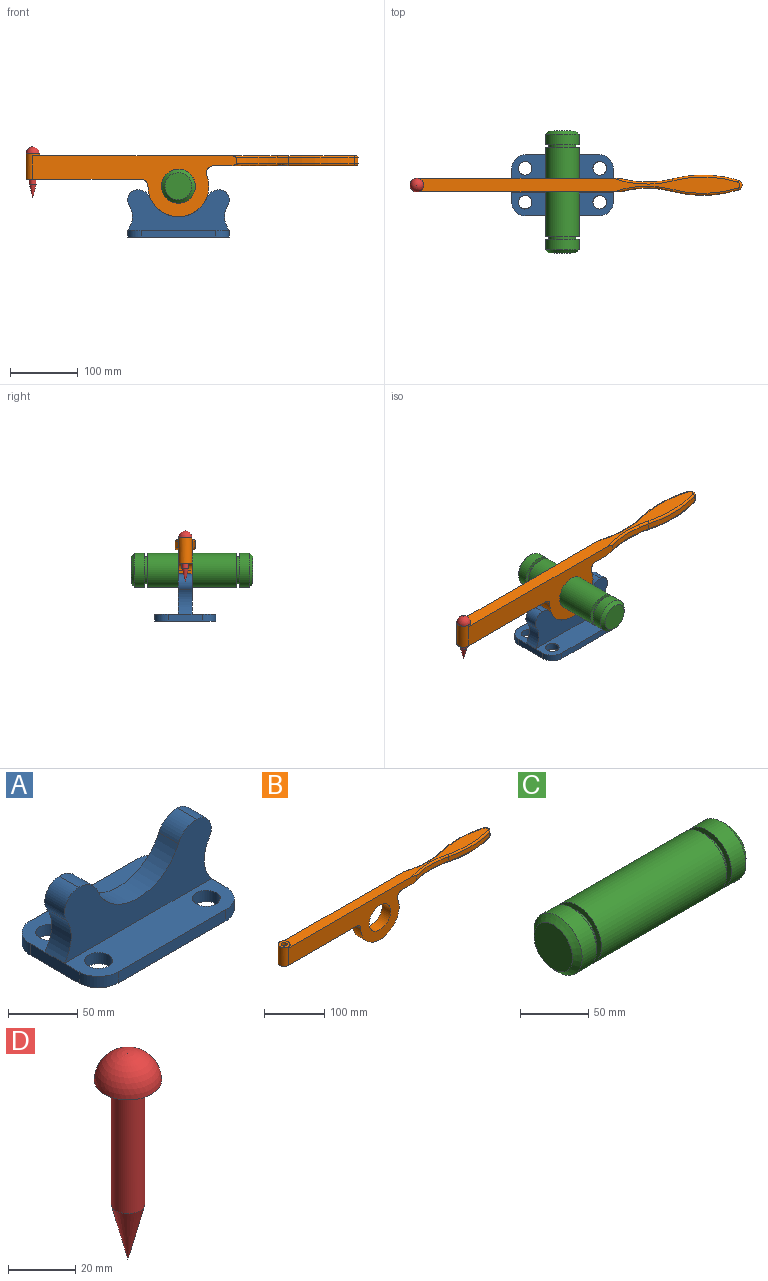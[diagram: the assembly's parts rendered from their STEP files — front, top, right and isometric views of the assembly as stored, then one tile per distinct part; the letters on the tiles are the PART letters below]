
ASSEMBLY  parts=4 mates=4
PART A: 24 faces, bbox 150x90x69.7 mm
  f0: plane 150x35mm, normal (0,0,1), area 4450mm2, adj f1,f2,f3,f4,f5,f8,f9,f23
  f1: plane 50x10mm, normal (1,0,0), area 500mm2, adj f0,f2,f12,f13,f14,f18
  f2: cylinder r=20mm len=20mm, axis (0,0,-1), area 314.2mm2, adj f0,f1,f3,f14
  f3: plane 110x10mm, normal (0,1,0), area 1100mm2, adj f0,f2,f4,f14
  f4: cylinder r=20mm len=20mm, axis (0,0,-1), area 314.2mm2, adj f0,f3,f5,f14
  f5: plane 50x10mm, normal (-1,0,0), area 500mm2, adj f0,f4,f6,f13,f14,f17
  f6: cylinder r=20mm len=20mm, axis (0,0,-1), area 314.2mm2, adj f5,f7,f13,f14
  f7: plane 110x10mm, normal (0,-1,0), area 1100mm2, adj f6,f12,f13,f14
  f8: cylinder r=10mm len=20mm, axis (0,0,-1), area 628.3mm2, adj f0,f14
  f9: cylinder r=10mm len=20mm, axis (0,0,-1), area 628.3mm2, adj f0,f14
  f10: cylinder r=10mm len=20mm, axis (0,0,-1), area 628.3mm2, adj f13,f14
  f11: cylinder r=10mm len=20mm, axis (0,0,-1), area 628.3mm2, adj f13,f14
  f12: cylinder r=20mm len=20mm, axis (0,0,-1), area 314.2mm2, adj f1,f7,f13,f14
  f13: plane 150x35mm, normal (0,0,1), area 4450mm2, adj f1,f5,f6,f7,f10,f11,f12,f22
  f14: plane 150x90mm, normal (0,0,-1), area 11900mm2, adj f1,f2,f3,f4,f5,f6,f7,f8
  f15: cylinder r=20mm len=20mm, axis (0,1,0), area 478.2mm2, adj f16,f21,f22,f23
  f16: cylinder r=15mm len=22.88mm, axis (0,1,0), area 630.1mm2, adj f15,f17,f22,f23
  f17: cylinder r=32mm len=36.82mm, axis (0,1,0), area 786.4mm2, adj f5,f16,f22,f23
  f18: cylinder r=32mm len=36.82mm, axis (0,1,0), area 786.4mm2, adj f1,f19,f22,f23
  f19: cylinder r=15mm len=22.88mm, axis (0,1,0), area 630.1mm2, adj f18,f20,f22,f23
  f20: cylinder r=20mm len=20mm, axis (0,1,0), area 478.2mm2, adj f19,f21,f22,f23
  f21: cylinder r=45mm len=82.91mm, axis (0,1,0), area 2108.2mm2, adj f15,f20,f22,f23
  f22: plane 150x59.71mm, normal (0,-1,0), area 5688.6mm2, adj f13,f15,f16,f17,f18,f19,f20,f21
  f23: plane 150x59.71mm, normal (0,1,0), area 5688.6mm2, adj f0,f15,f16,f17,f18,f19,f20,f21
PART B: 27 faces, bbox 490.6x59.7x93 mm
  f0: plane 477x24mm, normal (0,0,1), area 8212.2mm2, adj f7,f8,f19,f20,f21,f22,f23,f24
  f1: plane 170x20mm, normal (0,0,-1), area 3278.5mm2, adj f2,f7,f8,f24,f26
  f2: cylinder r=10mm len=20mm, axis (0,1,0), area 314.2mm2, adj f1,f3,f7,f8
  f3: cylinder r=45mm len=90mm, axis (0,1,0), area 3162.4mm2, adj f2,f4,f7,f8
  f4: cylinder r=10mm len=20mm, axis (0,1,0), area 388.6mm2, adj f3,f5,f7,f8
  f5: plane 210.77x24mm, normal (0,0,-1), area 3044.6mm2, adj f4,f7,f8,f14,f15,f16,f17,f18
  f6: cylinder r=25mm len=50mm, axis (0,1,0), area 3141.6mm2, adj f7,f8
  f7: plane 300x90mm, normal (0,-1,0), area 11779.4mm2, adj f0,f1,f2,f3,f4,f5,f6,f10
  f8: plane 300x90mm, normal (0,1,0), area 11779.4mm2, adj f0,f1,f2,f3,f4,f5,f6,f9
  f9: cylinder r=150mm len=77.32mm, axis (0,0,1), area 703.9mm2, adj f8,f13,f18,f23
  f10: cylinder r=150mm len=77.32mm, axis (0,0,1), area 703.9mm2, adj f7,f11,f14,f19
  f11: cylinder r=180mm len=97.36mm, axis (0,0,1), area 887.5mm2, adj f10,f12,f15,f20
  f12: cylinder r=7.5mm len=14.35mm, axis (0,0,1), area 172.1mm2, adj f11,f13,f16,f21
  f13: cylinder r=180mm len=97.36mm, axis (0,0,1), area 887.5mm2, adj f9,f12,f17,f22
  f14: torus R=153mm, axis (0,0,-1), area 388.6mm2, adj f5,f7,f10,f15
  f15: torus R=177mm, axis (0,0,-1), area 461.9mm2, adj f5,f11,f14,f16
  f16: torus R=4.5mm, axis (0,0,-1), area 77mm2, adj f5,f12,f15,f17
  f17: torus R=177mm, axis (0,0,-1), area 461.9mm2, adj f5,f13,f16,f18
  f18: torus R=153mm, axis (0,0,-1), area 388.6mm2, adj f5,f8,f9,f17
  f19: torus R=153mm, axis (0,0,1), area 388.6mm2, adj f0,f7,f10,f20
  f20: torus R=177mm, axis (0,0,1), area 461.9mm2, adj f0,f11,f19,f21
  f21: torus R=4.5mm, axis (0,0,1), area 77mm2, adj f0,f12,f20,f22
  f22: torus R=177mm, axis (0,0,1), area 461.9mm2, adj f0,f13,f21,f23
  f23: torus R=153mm, axis (0,0,1), area 388.6mm2, adj f0,f8,f9,f22
  f24: cylinder r=10mm len=38mm, axis (0,0,1), area 1288.1mm2, adj f0,f1,f7,f8,f25
  f25: plane 20x20mm, normal (0,0,1), area 235.6mm2, adj f24,f26
  f26: cylinder r=5mm len=38mm, axis (0,0,1), area 1193.8mm2, adj f1,f25
PART C: 13 faces, bbox 180x50x50 mm
  f0: plane 50x50mm, normal (1,0,0), area 706.9mm2, adj f1,f10
  f1: cylinder r=25mm len=50mm, axis (-1,0,0), area 2356.2mm2, adj f0,f12
  f2: plane 40x40mm, normal (-1,0,0), area 1256.6mm2, adj f12
  f3: plane 40x40mm, normal (1,0,0), area 1256.6mm2, adj f11
  f4: cylinder r=25mm len=50mm, axis (-1,0,0), area 2356.2mm2, adj f5,f11
  f5: plane 50x50mm, normal (-1,0,0), area 706.9mm2, adj f4,f6
  f6: cylinder r=20mm len=40mm, axis (-1,0,0), area 628.3mm2, adj f5,f7
  f7: plane 50x50mm, normal (1,0,0), area 706.9mm2, adj f6,f8
  f8: cylinder r=25mm len=130mm, axis (-1,0,0), area 20420.4mm2, adj f7,f9
  f9: plane 50x50mm, normal (-1,0,0), area 706.9mm2, adj f8,f10
  f10: cylinder r=20mm len=40mm, axis (-1,0,0), area 628.3mm2, adj f0,f9
  f11: cone r=25mm half-angle=45deg, axis (-1,0,0), area 999.6mm2, adj f3,f4
  f12: cone r=20mm half-angle=45deg, axis (1,0,0), area 999.6mm2, adj f1,f2
PART D: 4 faces, bbox 20x20x75 mm
  f0: plane 20x20mm, normal (0,0,-1), area 235.6mm2, adj f1,f3
  f1: cylinder r=5mm len=45mm, axis (0,0,-1), area 1413.7mm2, adj f0,f2
  f2: cone r=5mm half-angle=14deg, axis (0,0,1), area 323.8mm2, adj f1
  f3: sphere r=10mm, area 628.3mm2, adj f0
PLACE A t=(-118.31,-101.96,-50.47)mm fixed
PLACE B t=(-118.31,-101.96,24.53)mm
PLACE C rot(axis=(0.58,-0.58,-0.58),120deg) t=(-118.31,-111.96,24.53)mm
PLACE D t=(-333.31,-101.96,27.53)mm
MATE cylindrical B.f6 <-> C.f1  axis (0,-1,0) through (-118.31,-111.96,24.53)mm
MATE revolute A.f21 <-> B.f3  axis (0,1,0) through (-118.31,-101.96,24.53)mm
MATE slider B.f26 <-> D.f1  axis (0,0,1) through (-333.31,-101.96,72.53)mm
MATE planar D.f1 <-> B.f24  axis (0,0,-1) through (-333.31,-101.96,72.53)mm
